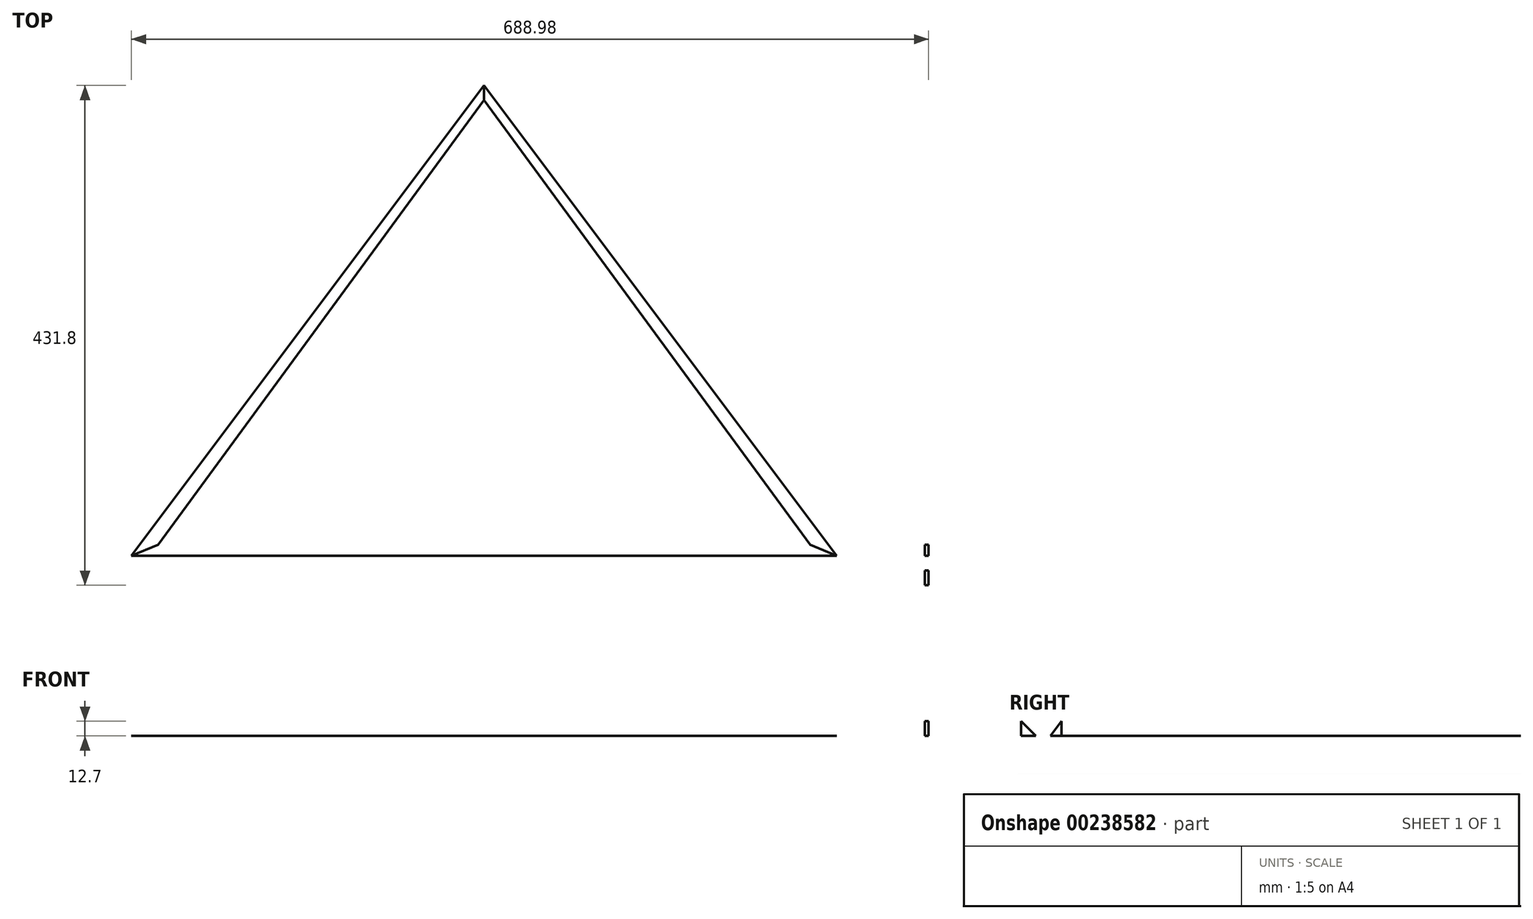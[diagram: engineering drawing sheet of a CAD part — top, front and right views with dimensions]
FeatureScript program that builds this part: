
annotation { "Feature Type Name" : "Feature", "Feature Type Description" : "" }
export const myFeature = defineFeature(function(context is Context, id is Id, definition is map)
    precondition{}
    {
        {
            assignVariable(context, id + "F0", {"name" : "l", "anyValue" : 609.6 * mm});
        }
        {
            var Q0;
            Q0=qCreatedBy(makeId("Top.planeOp"),FACE);
            var sketch = newSketch(context, id + "F1", { "sketchPlane" : qUnion([Q0])});
            skLineSegment(sketch, "E0", {"start": v(0, 0) * mm, "end": v(304.8, 0) * mm});
            skLineSegment(sketch, "E1", {"start": v(0, 0) * mm, "end": v(-304.8, 0) * mm});
            skLineSegment(sketch, "E2", {"start": v(0, 0) * mm, "end": v(0, 406.4) * mm, "construction": true});
            skLineSegment(sketch, "E3", {"start": v(0, 406.4) * mm, "end": v(304.8, 0) * mm});
            skLineSegment(sketch, "E4", {"start": v(0, 406.4) * mm, "end": v(-304.8, 0) * mm});
            skSolve(sketch);
        }
        {
            assignVariable(context, id + "F2", {"name" : "th", "anyValue" : 1 / 50.8 * mm});
        }
        {
            var Q0;
            Q0=qCreatedBy(makeId("Front.planeOp"),FACE);
            var sketch = newSketch(context, id + "F3", { "sketchPlane" : qUnion([Q0])});
            skLineSegment(sketch, "E5.0", {"start": v(0, 0) * mm, "end": v(-304.8, 0) * mm, "construction": true});
            skLineSegment(sketch, "E6.0", {"start": v(0, 0) * mm, "end": v(304.8, 0) * mm, "construction": true});
            skLineSegment(sketch, "E7", {"start": v(-304.8, 0) * mm, "end": v(234.02, 538.82) * mm, "construction": true});
            skLineSegment(sketch, "E8", {"start": v(304.8, 0) * mm, "end": v(-234.02, 538.82) * mm, "construction": true});
            skPoint(sketch, "E9", {"position": v(-292.1, 12.7) * mm});
            skPoint(sketch, "E10", {"position": v(292.1, 12.7) * mm});
            skSolve(sketch);
        }
        {
            var Q0;
            Q0=qCreatedBy(makeId("Top.planeOp"),FACE);
            cPlane(context, id + "F4", {"entities" : qUnion([Q0]), "cplaneType" : CPlaneType.OFFSET, "offset" : getVariable(context, 'th'), "width" : 152.4 * mm, "height" : 152.4 * mm});
        }
        {
            var Q0;
            Q0=qCreatedBy(makeId("Right.planeOp"),FACE);
            var sketch = newSketch(context, id + "F5", { "sketchPlane" : qUnion([Q0])});
            skLineSegment(sketch, "E11", {"start": v(0, 0) * mm, "end": v(9.52, 12.7) * mm});
            skLineSegment(sketch, "E12", {"start": v(9.52, 12.7) * mm, "end": v(9.52, 0) * mm});
            skLineSegment(sketch, "E13", {"start": v(9.52, 0) * mm, "end": v(0, 0) * mm});
            skSolve(sketch);
        }
        {
            var Q0;
            Q0=qCreatedBy(id+"F4.planeOp",FACE);
            var sketch = newSketch(context, id + "F6", { "sketchPlane" : qUnion([Q0])});
            skLineSegment(sketch, "E14", {"start": v(0, 0) * mm, "end": v(0, 9.52) * mm});
            skPoint(sketch, "E15", {"position": v(-281.78, 9.52) * mm});
            skPoint(sketch, "E16.0", {"position": v(-304.8, 0) * mm});
            skPoint(sketch, "E17.0", {"position": v(0, 406.4) * mm});
            skPoint(sketch, "E18.0", {"position": v(304.8, 0) * mm});
            skPoint(sketch, "E19", {"position": v(0, 393.7) * mm});
            skPoint(sketch, "E20", {"position": v(281.78, 9.52) * mm});
            skLineSegment(sketch, "E21", {"start": v(-281.78, 9.52) * mm, "end": v(0, 393.7) * mm});
            skLineSegment(sketch, "E22", {"start": v(0, 393.7) * mm, "end": v(281.78, 9.52) * mm});
            skLineSegment(sketch, "E23", {"start": v(281.78, 9.52) * mm, "end": v(-281.78, 9.52) * mm});
            skSolve(sketch);
        }
        {
            var Q0;
            Q0 = qSketchRegion(id + "F6", true);
            var Q1;
            Q1 = qSketchRegion(id + "F1", true);
            loft(context, id + "F7", {"sheetProfilesArray" : [{ "sheetProfileEntities" : qUnion([Q0]) }, { "sheetProfileEntities" : qUnion([Q1]) }]});
        }
        {
            var Q0;
            Q0=qCreatedBy(makeId("Right.planeOp"),FACE);
            cPlane(context, id + "F8", {"entities" : qUnion([Q0]), "cplaneType" : CPlaneType.OFFSET, "offset" : (getVariable(context, 'l')) * 5 / 8, "width" : 152.4 * mm, "height" : 152.4 * mm});
        }
        {
            var Q0;
            Q0=qCreatedBy(id+"F8.planeOp",FACE);
            var sketch = newSketch(context, id + "F9", { "sketchPlane" : qUnion([Q0])});
            skLineSegment(sketch, "E24.0", {"start": v(9.52, 12.7) * mm, "end": v(9.52, 0) * mm});
            skLineSegment(sketch, "E25.0", {"start": v(0, 0) * mm, "end": v(9.52, 12.7) * mm});
            skLineSegment(sketch, "E26.0", {"start": v(9.52, 0) * mm, "end": v(0, 0) * mm});
            skPoint(sketch, "E27", {"position": v(-12.7, 0) * mm});
            skLineSegment(sketch, "E28", {"start": v(-12.7, 0) * mm, "end": v(-25.4, 0) * mm});
            skLineSegment(sketch, "E29", {"start": v(-25.4, 0) * mm, "end": v(-25.4, 12.7) * mm});
            skLineSegment(sketch, "E30", {"start": v(-25.4, 12.7) * mm, "end": v(-12.7, 0) * mm});
            skSolve(sketch);
        }
        {
            var Q0;
            Q0 = qSketchRegion(id + "F9", true);
            extrude(context, id + "F10", {"entities" : qUnion([Q0]), "depth" : 3.17 * mm, "offsetDistance" : 25.4 * mm});
        }
    });
